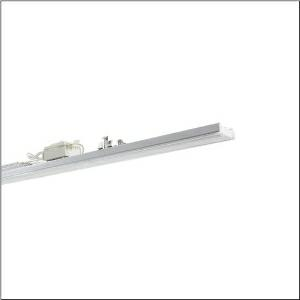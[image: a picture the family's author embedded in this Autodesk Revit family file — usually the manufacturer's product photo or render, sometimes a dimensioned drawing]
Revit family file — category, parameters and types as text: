
# Revit family: licross_11_recessed_ho_51tl18mn4d5m
name_source: partatom
category: Lighting Fixtures
units: mm (PartAtom-declared; Revit-internal decimal feet)

## family parameters
Cut with Voids When Loaded = No
Host = Face
Light Source = No
Part Type = Normal
Room Calculation Point = No
Round Connector Dimension = Use Diameter
Shared = No

## types (1)
- --- (1 x LED, 13950 lm, 74.5 W, 4000K)
    Apparent Load = 75 VA
    CIE Flux Codes = 78 94 99 100 100
    Color Rendering = 80
    Color Temperature = 4000K
    Default Elevation = 1800 mm
    Description = Licross 11 Recessed HO, luminaire insert, of sheet steel, coil coated, white, length: 1.500mm, width: 66mm, height: 67mm, LED rated luminous flux: 13.950lm, light colour: 840, SDCM (Standard Deviation of Colour Matching)MacAdam ≤ 2 SDCM (initial), control gear: ON/OFF Multilumen, with plug, 3-pole, with phase selection, mains connection: 220..240V, AC, 50/60Hz, rated input power: 75W, internal wiring halogen-free, primary light control with lens, of plastic, primary optical cover: cover, of PMMA, light emission: direct distribution, primary light characteristic: symmetric, protection rating (complete): IP40, insulation class (complete): insulation class I (protective earthing), certification: CE, ENEC, VDE, UKCA, protection symbol: D if used in an environment without relevant dust loads with corresponding accessories, impact resistance: IK06, permissible ambient temperature for indoor applications: -35..+35°C, corresponds to IFS (International Featured Standards) requirements for safety and quality in the food industry, reducing of maximum allowable ambient temperature of 5°C with ceiling mounting, The light source and the operating device comply with the requirements of the Ecodesign Regulation (EU) 2019/2020 and are replaceable in accordance with this regulation, packaging unit: 1 piece
    Height = 58 mm
    Lamp = 1 x LED
    Lamp Light Flux = 13950 lm
    Lamp Power = 74.5 W
    Lamp count = 1
    Length = 1500 mm
    Luminous efficacy = 187 lm/W
    Manufacturer = Siteco
    ModVariant = No
    Model = 51TL18MN4D5M
    Mounting Place = Ceiling
    Mounting Type = Pendant
    Number of Poles = 1
    OnlyDefault = Yes
    Power Factor = 1
    Product Name = Licross 11 Recessed HO
    Product group = luminaire insert | ceiling pendant
    ProductGroupID = 901
    Protection Class = Protection class I
    Protection Degree = IP 40
    RLX_Detail_Level = 1
    RLX_Emergency_Light_Flux = 0 lm
    RLX_Emergency_Type = 0
    RLX_Emergency_Type_DB = No
    RlxData = <blob elided: 22525 chars, md5=3863d9dd>
    Socket = socket
    Standby Power = 0 W
    System Light Flux = 13950 lm
    System Power = 75 W
    Type Comments = factory setting: luminous flux: 100 % | (A | C | E) | 174 mA
    Type Image = l_1296930.jpg
    URL = http://relux.com
    VarID = @adj_089583
    Voltage = 0 V
    Weight = 0.00 kg
    Width = 66 mm

## geometry (parser evidence)
native form markers: Blend x4, Sweep x10
no freeform markers — native parametric forms only
